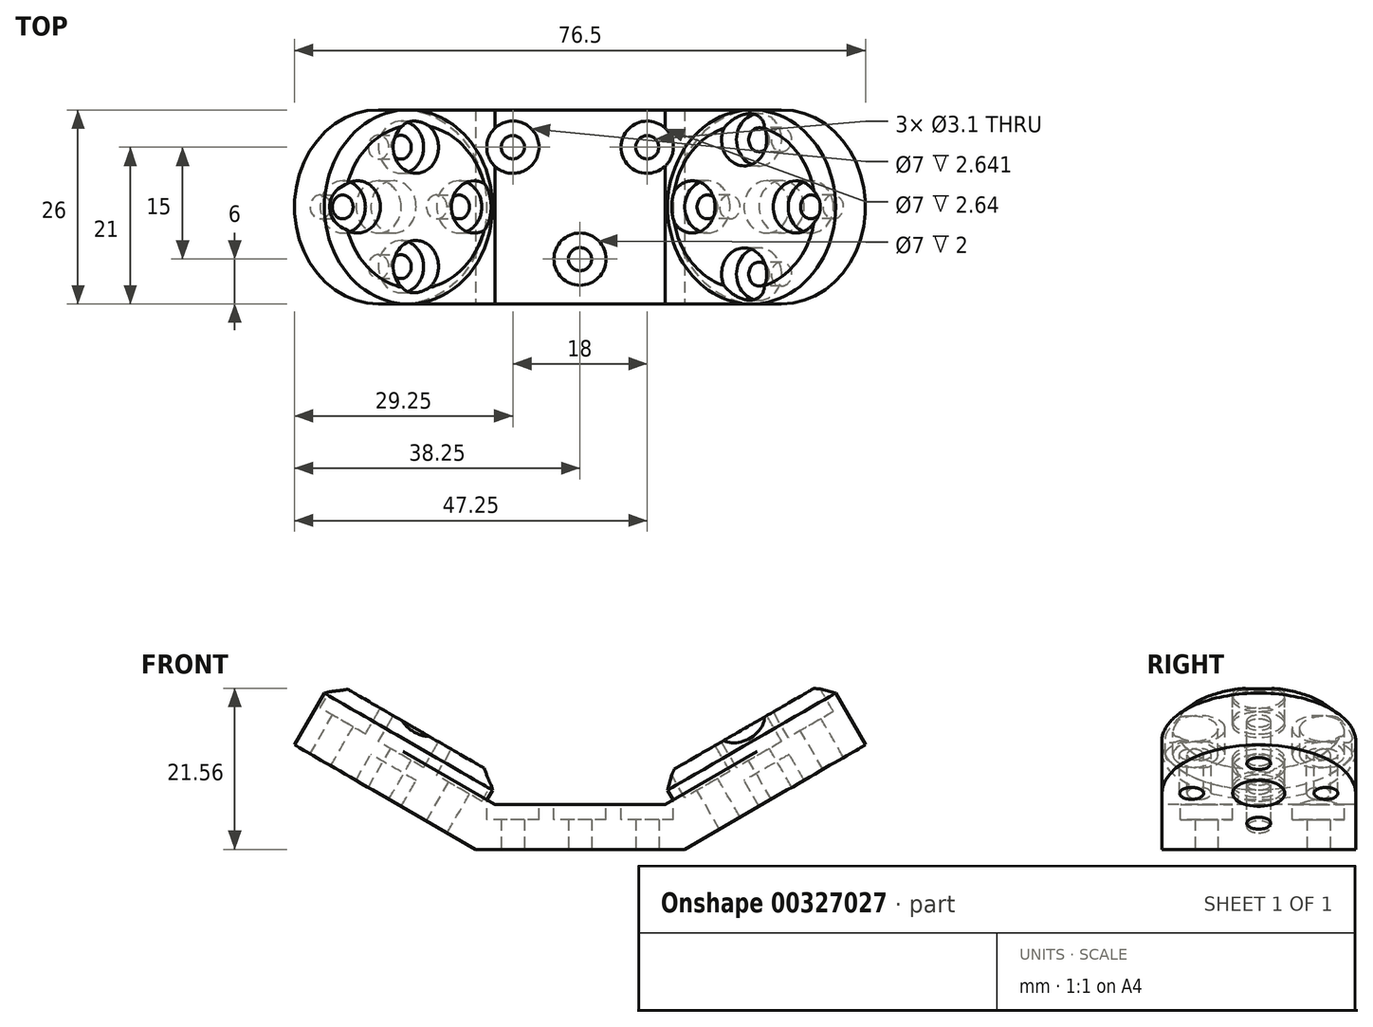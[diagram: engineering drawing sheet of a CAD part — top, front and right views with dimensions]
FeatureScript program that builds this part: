
annotation { "Feature Type Name" : "Feature", "Feature Type Description" : "" }
export const myFeature = defineFeature(function(context is Context, id is Id, definition is map)
    precondition{}
    {
        {
            var Q0;
            Q0=qCreatedBy(makeId("Top.planeOp"),FACE);
            var sketch = newSketch(context, id + "F0", { "sketchPlane" : qUnion([Q0])});
            skLineSegment(sketch, "E0.bottom", {"start": v(14, 13) * mm, "end": v(-14, 13) * mm});
            skLineSegment(sketch, "E0.top", {"start": v(14, -13) * mm, "end": v(-14, -13) * mm});
            skLineSegment(sketch, "E0.left", {"start": v(14, 13) * mm, "end": v(14, -13) * mm});
            skLineSegment(sketch, "E0.right", {"start": v(-14, 13) * mm, "end": v(-14, -13) * mm});
            skPoint(sketch, "E0.middle", {"position": v(0, 0) * mm});
            skCircle(sketch, "E1", {"center": v(9, 8) * mm, "radius": 1.55 * mm});
            skCircle(sketch, "E2", {"center": v(0, -7) * mm, "radius": 1.55 * mm});
            skCircle(sketch, "E3.MirrorC", {"center": v(-9, 8) * mm, "radius": 1.55 * mm});
            skSolve(sketch);
        }
        {
            var Q0;
            Q0=makeQuery(id+"F0.imprint","IMPRINT",FACE,{"disambiguationData":[TD([[makeQuery(id+"F0.imprint","IMPRINT",EDGE,{"derivedFrom":sQuery(id+"F0.wireOp",EDGE,"E0.bottom")}),1.0]])]});
            extrude(context, id + "F1", {"entities" : qUnion([Q0]), "depth" : 6 * mm});
        }
        {
            var Q0;
            Q0=makeQuery(id+"F1.opExtrude","SWEPT_FACE",FACE,{"disambiguationData":[OSD([sQuery(id+"F0.wireOp",EDGE,"E0.top")])]});
            var sketch = newSketch(context, id + "F2", { "sketchPlane" : qUnion([Q0])});
            skLineSegment(sketch, "E4", {"start": v(14, 0) * mm, "end": v(31.32, 10) * mm});
            skSolve(sketch);
        }
        {
            var Q0;
            Q0=sQuery(id+"F2.wireOp",EDGE,"E4");
            var Q1;
            Q1=makeQuery(id+"F1.opExtrude","SWEPT_FACE",FACE,{"disambiguationData":[OSD([sQuery(id+"F0.wireOp",EDGE,"E0.left")])]});
            cPlane(context, id + "F3", {"entities" : qUnion([Q0, Q1]), "cplaneType" : CPlaneType.LINE_ANGLE, "offset" : 25 * mm, "angle" : 0 * degree, "width" : 150 * mm, "height" : 150 * mm});
        }
        {
            var Q0;
            Q0=qCreatedBy(id+"F3.planeOp",FACE);
            var sketch = newSketch(context, id + "F4", { "sketchPlane" : qUnion([Q0])});
            skLineSegment(sketch, "E5", {"start": v(27.12, -13) * mm, "end": v(12.12, -13) * mm});
            skLineSegment(sketch, "E6", {"start": v(12.12, 13) * mm, "end": v(27.12, 13) * mm});
            skCircle(sketch, "E7", {"center": v(27.12, 0) * mm, "radius": 13 * mm});
            skLineSegment(sketch, "E8", {"start": v(12.12, 13) * mm, "end": v(12.12, -13) * mm});
            skSolve(sketch);
        }
        {
            var Q0;
            Q0 = qSketchRegion(id + "F4", true);
            extrude(context, id + "F5", {"entities" : qUnion([Q0]), "operationType" : NewBodyOperationType.ADD, "depth" : 6.5 * mm});
        }
        {
            var Q0;
            {var subQ0=sQuery(id+"F4.wireOp",EDGE,"E7");var subQ1=makeQuery(id+"F4.imprint","INTERSECT",VERTEX,{"derivedFrom":[sQuery(id+"F4.wireOp",EDGE,"E5"),subQ0]});Q0=makeQuery(id+"F4.imprint","IMPRINT",FACE,{"disambiguationData":[TD([[makeQuery(id+"F4.imprint","IMPRINT",EDGE,{"disambiguationData":[TD([[subQ1,1.0]])],"derivedFrom":subQ0}),1.0]])]});}
            extrude(context, id + "F6", {"entities" : qUnion([Q0]), "operationType" : NewBodyOperationType.ADD, "depth" : 10 * mm});
        }
        {
            var Q0;
            Q0=makeQuery(id+"F6.opExtrude","CAP_EDGE",EDGE,{"disambiguationData":[OSD([sQuery(id+"F4.wireOp",EDGE,"E7")])],"isStart":false});
            chamfer(context, id + "F7", {"entities" : qUnion([Q0]), "width" : 2 * mm, "tangentPropagation" : true});
        }
        {
            var Q0;
            Q0=makeQuery(id+"F1.opExtrude","SWEPT_BODY",BODY,{"disambiguationData":[OSD([sQuery(id+"F0.wireOp",EDGE,"E0.bottom"),sQuery(id+"F0.wireOp",EDGE,"E0.top"),sQuery(id+"F0.wireOp",EDGE,"E0.left"),sQuery(id+"F0.wireOp",EDGE,"E0.right"),sQuery(id+"F0.wireOp",EDGE,"E1"),sQuery(id+"F0.wireOp",EDGE,"E2"),sQuery(id+"F0.wireOp",EDGE,"E3.MirrorC")])]});
            var Q1;
            Q1=qCreatedBy(makeId("Right.planeOp"),FACE);
            mirror(context, id + "F8", {"operationType" : NewBodyOperationType.ADD, "entities" : qUnion([Q0]), "mirrorPlane" : qUnion([Q1])});
        }
        {
            var Q0;
            Q0=makeQuery(id+"F6.opExtrude","CAP_FACE",FACE,{"disambiguationData":[OSD([sQuery(id+"F4.wireOp",EDGE,"E7")])],"isStart":false});
            var sketch = newSketch(context, id + "F9", { "sketchPlane" : qUnion([Q0])});
            skCircle(sketch, "E9", {"center": v(27.12, 0) * mm, "radius": 3.5 * mm});
            skCircle(sketch, "E10", {"center": v(19.12, 0) * mm, "radius": 1.6 * mm});
            skCircle(sketch, "E11", {"center": v(35.12, 0) * mm, "radius": 1.6 * mm});
            skCircle(sketch, "E12", {"center": v(27.12, -9) * mm, "radius": 1.6 * mm});
            skCircle(sketch, "E13", {"center": v(27.12, 9) * mm, "radius": 1.6 * mm});
            skCircle(sketch, "E14", {"center": v(35.12, 0) * mm, "radius": 3.5 * mm});
            skCircle(sketch, "E15", {"center": v(27.12, -9) * mm, "radius": 3.5 * mm});
            skCircle(sketch, "E16", {"center": v(19.12, 0) * mm, "radius": 3.5 * mm});
            skCircle(sketch, "E17", {"center": v(27.12, 9) * mm, "radius": 3.5 * mm});
            skSolve(sketch);
        }
        {
            var Q0;
            Q0=makeQuery(id+"F9.imprint","IMPRINT",FACE,{"disambiguationData":[TD([[makeQuery(id+"F9.imprint","IMPRINT",EDGE,{"derivedFrom":sQuery(id+"F9.wireOp",EDGE,"E12")}),-1.0]])]});
            var Q1;
            {var subQ0=sQuery(id+"F9.wireOp",EDGE,"E15");var subQ1=sQuery(id+"F4.wireOp",EDGE,"E7");var subQ2=makeQuery(id+"F7.opChamfer","BLEND_EDGE",EDGE,{"blendedFrom":[makeQuery(id+"F6.opExtrude","CAP_EDGE",EDGE,{"disambiguationData":[OSD([subQ1])],"isStart":false}),makeQuery(id+"F6.opExtrude","CAP_FACE",FACE,{"disambiguationData":[OSD([subQ1])],"isStart":false})],"blendedInto":[makeQuery(id+"F6.opExtrude","CAP_FACE",FACE,{"disambiguationData":[OSD([subQ1])],"isStart":false})]});var subQ3=makeQuery(id+"F9.imprint","INTERSECT",VERTEX,{"disambiguationData":[OD(0.0)],"derivedFrom":[subQ2,subQ0]});Q1=makeQuery(id+"F9.imprint","IMPRINT",FACE,{"disambiguationData":[TD([[makeQuery(id+"F9.imprint","IMPRINT",EDGE,{"disambiguationData":[TD([[subQ3,-1.0]])],"derivedFrom":subQ0}),1.0]])]});}
            var Q2;
            Q2=makeQuery(id+"F9.imprint","IMPRINT",FACE,{"disambiguationData":[TD([[makeQuery(id+"F9.imprint","IMPRINT",EDGE,{"derivedFrom":sQuery(id+"F9.wireOp",EDGE,"E10")}),-1.0]])]});
            var Q3;
            {var subQ0=sQuery(id+"F9.wireOp",EDGE,"E16");var subQ1=sQuery(id+"F4.wireOp",EDGE,"E7");var subQ2=makeQuery(id+"F7.opChamfer","BLEND_EDGE",EDGE,{"blendedFrom":[makeQuery(id+"F6.opExtrude","CAP_EDGE",EDGE,{"disambiguationData":[OSD([subQ1])],"isStart":false}),makeQuery(id+"F6.opExtrude","CAP_FACE",FACE,{"disambiguationData":[OSD([subQ1])],"isStart":false})],"blendedInto":[makeQuery(id+"F6.opExtrude","CAP_FACE",FACE,{"disambiguationData":[OSD([subQ1])],"isStart":false})]});var subQ3=makeQuery(id+"F9.imprint","INTERSECT",VERTEX,{"disambiguationData":[OD(0.0)],"derivedFrom":[subQ2,subQ0]});Q3=makeQuery(id+"F9.imprint","IMPRINT",FACE,{"disambiguationData":[TD([[makeQuery(id+"F9.imprint","IMPRINT",EDGE,{"disambiguationData":[TD([[subQ3,1.0]])],"derivedFrom":subQ0}),1.0]])]});}
            var Q4;
            Q4=makeQuery(id+"F9.imprint","IMPRINT",FACE,{"disambiguationData":[TD([[makeQuery(id+"F9.imprint","IMPRINT",EDGE,{"derivedFrom":sQuery(id+"F9.wireOp",EDGE,"E13")}),-1.0]])]});
            var Q5;
            {var subQ0=sQuery(id+"F9.wireOp",EDGE,"E17");var subQ1=sQuery(id+"F4.wireOp",EDGE,"E7");var subQ2=makeQuery(id+"F7.opChamfer","BLEND_EDGE",EDGE,{"blendedFrom":[makeQuery(id+"F6.opExtrude","CAP_EDGE",EDGE,{"disambiguationData":[OSD([subQ1])],"isStart":false}),makeQuery(id+"F6.opExtrude","CAP_FACE",FACE,{"disambiguationData":[OSD([subQ1])],"isStart":false})],"blendedInto":[makeQuery(id+"F6.opExtrude","CAP_FACE",FACE,{"disambiguationData":[OSD([subQ1])],"isStart":false})]});var subQ3=makeQuery(id+"F9.imprint","INTERSECT",VERTEX,{"disambiguationData":[OD(0.0)],"derivedFrom":[subQ2,subQ0]});Q5=makeQuery(id+"F9.imprint","IMPRINT",FACE,{"disambiguationData":[TD([[makeQuery(id+"F9.imprint","IMPRINT",EDGE,{"disambiguationData":[TD([[subQ3,1.0]])],"derivedFrom":subQ0}),1.0]])]});}
            var Q6;
            Q6=makeQuery(id+"F9.imprint","IMPRINT",FACE,{"disambiguationData":[TD([[makeQuery(id+"F9.imprint","IMPRINT",EDGE,{"derivedFrom":sQuery(id+"F9.wireOp",EDGE,"E11")}),-1.0]])]});
            var Q7;
            {var subQ0=sQuery(id+"F9.wireOp",EDGE,"E14");var subQ1=sQuery(id+"F4.wireOp",EDGE,"E7");var subQ2=makeQuery(id+"F7.opChamfer","BLEND_EDGE",EDGE,{"blendedFrom":[makeQuery(id+"F6.opExtrude","CAP_EDGE",EDGE,{"disambiguationData":[OSD([subQ1])],"isStart":false}),makeQuery(id+"F6.opExtrude","CAP_FACE",FACE,{"disambiguationData":[OSD([subQ1])],"isStart":false})],"blendedInto":[makeQuery(id+"F6.opExtrude","CAP_FACE",FACE,{"disambiguationData":[OSD([subQ1])],"isStart":false})]});var subQ3=makeQuery(id+"F9.imprint","INTERSECT",VERTEX,{"disambiguationData":[OD(0.0)],"derivedFrom":[subQ2,subQ0]});Q7=makeQuery(id+"F9.imprint","IMPRINT",FACE,{"disambiguationData":[TD([[makeQuery(id+"F9.imprint","IMPRINT",EDGE,{"disambiguationData":[TD([[subQ3,-1.0]])],"derivedFrom":subQ0}),1.0]])]});}
            var Q8;
            Q8=makeQuery(id+"F9.imprint","IMPRINT",FACE,{"disambiguationData":[TD([[makeQuery(id+"F9.imprint","IMPRINT",EDGE,{"derivedFrom":sQuery(id+"F9.wireOp",EDGE,"E11")}),1.0]])]});
            var Q9;
            Q9=makeQuery(id+"F9.imprint","IMPRINT",FACE,{"disambiguationData":[TD([[makeQuery(id+"F9.imprint","IMPRINT",EDGE,{"derivedFrom":sQuery(id+"F9.wireOp",EDGE,"E10")}),1.0]])]});
            var Q10;
            Q10=makeQuery(id+"F9.imprint","IMPRINT",FACE,{"disambiguationData":[TD([[makeQuery(id+"F9.imprint","IMPRINT",EDGE,{"derivedFrom":sQuery(id+"F9.wireOp",EDGE,"E13")}),1.0]])]});
            var Q11;
            Q11=makeQuery(id+"F9.imprint","IMPRINT",FACE,{"disambiguationData":[TD([[makeQuery(id+"F9.imprint","IMPRINT",EDGE,{"derivedFrom":sQuery(id+"F9.wireOp",EDGE,"E12")}),1.0]])]});
            extrude(context, id + "F10", {"entities" : qUnion([Q0, Q1, Q2, Q3, Q4, Q5, Q6, Q7, Q8, Q9, Q10, Q11]), "operationType" : NewBodyOperationType.REMOVE, "oppositeDirection" : true, "depth" : 4 * mm});
        }
        {
            var Q0;
            Q0=makeQuery(id+"F9.imprint","IMPRINT",FACE,{"disambiguationData":[TD([[makeQuery(id+"F9.imprint","IMPRINT",EDGE,{"derivedFrom":sQuery(id+"F9.wireOp",EDGE,"E11")}),1.0]])]});
            var Q1;
            Q1=makeQuery(id+"F9.imprint","IMPRINT",FACE,{"disambiguationData":[TD([[makeQuery(id+"F9.imprint","IMPRINT",EDGE,{"derivedFrom":sQuery(id+"F9.wireOp",EDGE,"E10")}),1.0]])]});
            var Q2;
            Q2=makeQuery(id+"F9.imprint","IMPRINT",FACE,{"disambiguationData":[TD([[makeQuery(id+"F9.imprint","IMPRINT",EDGE,{"derivedFrom":sQuery(id+"F9.wireOp",EDGE,"E12")}),1.0]])]});
            var Q3;
            Q3=makeQuery(id+"F9.imprint","IMPRINT",FACE,{"disambiguationData":[TD([[makeQuery(id+"F9.imprint","IMPRINT",EDGE,{"derivedFrom":sQuery(id+"F9.wireOp",EDGE,"E13")}),1.0]])]});
            extrude(context, id + "F11", {"entities" : qUnion([Q0, Q1, Q2, Q3]), "operationType" : NewBodyOperationType.REMOVE, "oppositeDirection" : true, "depth" : 25 * mm});
        }
        {
            var Q0;
            Q0=makeQuery(id+"F9.imprint","IMPRINT",FACE,{"disambiguationData":[TD([[makeQuery(id+"F9.imprint","IMPRINT",EDGE,{"derivedFrom":sQuery(id+"F9.wireOp",EDGE,"E9")}),1.0]])]});
            extrude(context, id + "F12", {"entities" : qUnion([Q0]), "operationType" : NewBodyOperationType.REMOVE, "oppositeDirection" : true, "depth" : 25 * mm, "hasSecondDirection" : true, "secondDirectionOppositeDirection" : true, "secondDirectionDepth" : 6 * mm});
        }
        {
            var Q0;
            Q0=makeQuery(id+"F8.opPattern","COPY",FACE,{"derivedFrom":makeQuery(id+"F6.opExtrude","CAP_FACE",FACE,{"disambiguationData":[OSD([sQuery(id+"F4.wireOp",EDGE,"E7")])],"isStart":false}),"instanceName":"1"});
            var sketch = newSketch(context, id + "F13", { "sketchPlane" : qUnion([Q0])});
            skCircle(sketch, "E18", {"center": v(-27.12, 0) * mm, "radius": 3.5 * mm});
            skCircle(sketch, "E19", {"center": v(-36.12, 0) * mm, "radius": 1.6 * mm});
            skCircle(sketch, "E20", {"center": v(-18.12, 0) * mm, "radius": 1.6 * mm});
            skCircle(sketch, "E21", {"center": v(-27.12, -8) * mm, "radius": 1.6 * mm});
            skCircle(sketch, "E22", {"center": v(-27.12, 8) * mm, "radius": 1.6 * mm});
            skCircle(sketch, "E23", {"center": v(-27.12, -8) * mm, "radius": 3.5 * mm});
            skCircle(sketch, "E24", {"center": v(-36.12, 0) * mm, "radius": 3.5 * mm});
            skCircle(sketch, "E25", {"center": v(-27.12, 8) * mm, "radius": 3.5 * mm});
            skCircle(sketch, "E26", {"center": v(-18.12, 0) * mm, "radius": 3.5 * mm});
            skSolve(sketch);
        }
        {
            var Q0;
            Q0=makeQuery(id+"F13.imprint","IMPRINT",FACE,{"disambiguationData":[TD([[makeQuery(id+"F13.imprint","IMPRINT",EDGE,{"derivedFrom":sQuery(id+"F13.wireOp",EDGE,"E21")}),-1.0]])]});
            var Q1;
            Q1=makeQuery(id+"F13.imprint","IMPRINT",FACE,{"disambiguationData":[TD([[makeQuery(id+"F13.imprint","IMPRINT",EDGE,{"derivedFrom":sQuery(id+"F13.wireOp",EDGE,"E19")}),-1.0]])]});
            var Q2;
            Q2=makeQuery(id+"F13.imprint","IMPRINT",FACE,{"disambiguationData":[TD([[makeQuery(id+"F13.imprint","IMPRINT",EDGE,{"derivedFrom":sQuery(id+"F13.wireOp",EDGE,"E22")}),-1.0]])]});
            var Q3;
            Q3=makeQuery(id+"F13.imprint","IMPRINT",FACE,{"disambiguationData":[TD([[makeQuery(id+"F13.imprint","IMPRINT",EDGE,{"derivedFrom":sQuery(id+"F13.wireOp",EDGE,"E20")}),-1.0]])]});
            var Q4;
            Q4=makeQuery(id+"F13.imprint","IMPRINT",FACE,{"disambiguationData":[TD([[makeQuery(id+"F13.imprint","IMPRINT",EDGE,{"derivedFrom":sQuery(id+"F13.wireOp",EDGE,"E20")}),1.0]])]});
            var Q5;
            Q5=makeQuery(id+"F13.imprint","IMPRINT",FACE,{"disambiguationData":[TD([[makeQuery(id+"F13.imprint","IMPRINT",EDGE,{"derivedFrom":sQuery(id+"F13.wireOp",EDGE,"E22")}),1.0]])]});
            var Q6;
            Q6=makeQuery(id+"F13.imprint","IMPRINT",FACE,{"disambiguationData":[TD([[makeQuery(id+"F13.imprint","IMPRINT",EDGE,{"derivedFrom":sQuery(id+"F13.wireOp",EDGE,"E19")}),1.0]])]});
            var Q7;
            Q7=makeQuery(id+"F13.imprint","IMPRINT",FACE,{"disambiguationData":[TD([[makeQuery(id+"F13.imprint","IMPRINT",EDGE,{"derivedFrom":sQuery(id+"F13.wireOp",EDGE,"E21")}),1.0]])]});
            var Q8;
            {var subQ0=sQuery(id+"F13.wireOp",EDGE,"E23");var subQ1=sQuery(id+"F4.wireOp",EDGE,"E7");var subQ2=makeQuery(id+"F8.opPattern","COPY",EDGE,{"derivedFrom":makeQuery(id+"F7.opChamfer","BLEND_EDGE",EDGE,{"blendedFrom":[makeQuery(id+"F6.opExtrude","CAP_EDGE",EDGE,{"disambiguationData":[OSD([subQ1])],"isStart":false}),makeQuery(id+"F6.opExtrude","CAP_FACE",FACE,{"disambiguationData":[OSD([subQ1])],"isStart":false})],"blendedInto":[makeQuery(id+"F6.opExtrude","CAP_FACE",FACE,{"disambiguationData":[OSD([subQ1])],"isStart":false})]}),"instanceName":"1"});var subQ3=makeQuery(id+"F13.imprint","INTERSECT",VERTEX,{"disambiguationData":[OD(0.0)],"derivedFrom":[subQ2,subQ0]});Q8=makeQuery(id+"F13.imprint","IMPRINT",FACE,{"disambiguationData":[TD([[makeQuery(id+"F13.imprint","IMPRINT",EDGE,{"disambiguationData":[TD([[subQ3,-1.0]])],"derivedFrom":subQ0}),1.0]])]});}
            var Q9;
            {var subQ0=sQuery(id+"F13.wireOp",EDGE,"E24");var subQ1=sQuery(id+"F4.wireOp",EDGE,"E7");var subQ2=makeQuery(id+"F8.opPattern","COPY",EDGE,{"derivedFrom":makeQuery(id+"F7.opChamfer","BLEND_EDGE",EDGE,{"blendedFrom":[makeQuery(id+"F6.opExtrude","CAP_EDGE",EDGE,{"disambiguationData":[OSD([subQ1])],"isStart":false}),makeQuery(id+"F6.opExtrude","CAP_FACE",FACE,{"disambiguationData":[OSD([subQ1])],"isStart":false})],"blendedInto":[makeQuery(id+"F6.opExtrude","CAP_FACE",FACE,{"disambiguationData":[OSD([subQ1])],"isStart":false})]}),"instanceName":"1"});var subQ3=makeQuery(id+"F13.imprint","INTERSECT",VERTEX,{"disambiguationData":[OD(0.0)],"derivedFrom":[subQ2,subQ0]});Q9=makeQuery(id+"F13.imprint","IMPRINT",FACE,{"disambiguationData":[TD([[makeQuery(id+"F13.imprint","IMPRINT",EDGE,{"disambiguationData":[TD([[subQ3,1.0]])],"derivedFrom":subQ0}),1.0]])]});}
            var Q10;
            {var subQ0=sQuery(id+"F13.wireOp",EDGE,"E25");var subQ1=sQuery(id+"F4.wireOp",EDGE,"E7");var subQ2=makeQuery(id+"F8.opPattern","COPY",EDGE,{"derivedFrom":makeQuery(id+"F7.opChamfer","BLEND_EDGE",EDGE,{"blendedFrom":[makeQuery(id+"F6.opExtrude","CAP_EDGE",EDGE,{"disambiguationData":[OSD([subQ1])],"isStart":false}),makeQuery(id+"F6.opExtrude","CAP_FACE",FACE,{"disambiguationData":[OSD([subQ1])],"isStart":false})],"blendedInto":[makeQuery(id+"F6.opExtrude","CAP_FACE",FACE,{"disambiguationData":[OSD([subQ1])],"isStart":false})]}),"instanceName":"1"});var subQ3=makeQuery(id+"F13.imprint","INTERSECT",VERTEX,{"disambiguationData":[OD(0.0)],"derivedFrom":[subQ2,subQ0]});Q10=makeQuery(id+"F13.imprint","IMPRINT",FACE,{"disambiguationData":[TD([[makeQuery(id+"F13.imprint","IMPRINT",EDGE,{"disambiguationData":[TD([[subQ3,1.0]])],"derivedFrom":subQ0}),1.0]])]});}
            var Q11;
            {var subQ0=sQuery(id+"F13.wireOp",EDGE,"E26");var subQ1=sQuery(id+"F4.wireOp",EDGE,"E7");var subQ2=makeQuery(id+"F8.opPattern","COPY",EDGE,{"derivedFrom":makeQuery(id+"F7.opChamfer","BLEND_EDGE",EDGE,{"blendedFrom":[makeQuery(id+"F6.opExtrude","CAP_EDGE",EDGE,{"disambiguationData":[OSD([subQ1])],"isStart":false}),makeQuery(id+"F6.opExtrude","CAP_FACE",FACE,{"disambiguationData":[OSD([subQ1])],"isStart":false})],"blendedInto":[makeQuery(id+"F6.opExtrude","CAP_FACE",FACE,{"disambiguationData":[OSD([subQ1])],"isStart":false})]}),"instanceName":"1"});var subQ3=makeQuery(id+"F13.imprint","INTERSECT",VERTEX,{"disambiguationData":[OD(0.0)],"derivedFrom":[subQ2,subQ0]});Q11=makeQuery(id+"F13.imprint","IMPRINT",FACE,{"disambiguationData":[TD([[makeQuery(id+"F13.imprint","IMPRINT",EDGE,{"disambiguationData":[TD([[subQ3,-1.0]])],"derivedFrom":subQ0}),1.0]])]});}
            extrude(context, id + "F14", {"entities" : qUnion([Q0, Q1, Q2, Q3, Q4, Q5, Q6, Q7, Q8, Q9, Q10, Q11]), "operationType" : NewBodyOperationType.REMOVE, "oppositeDirection" : true, "depth" : 4 * mm});
        }
        {
            var Q0;
            Q0=makeQuery(id+"F13.imprint","IMPRINT",FACE,{"disambiguationData":[TD([[makeQuery(id+"F13.imprint","IMPRINT",EDGE,{"derivedFrom":sQuery(id+"F13.wireOp",EDGE,"E20")}),1.0]])]});
            var Q1;
            Q1=makeQuery(id+"F13.imprint","IMPRINT",FACE,{"disambiguationData":[TD([[makeQuery(id+"F13.imprint","IMPRINT",EDGE,{"derivedFrom":sQuery(id+"F13.wireOp",EDGE,"E21")}),1.0]])]});
            var Q2;
            Q2=makeQuery(id+"F13.imprint","IMPRINT",FACE,{"disambiguationData":[TD([[makeQuery(id+"F13.imprint","IMPRINT",EDGE,{"derivedFrom":sQuery(id+"F13.wireOp",EDGE,"E19")}),1.0]])]});
            var Q3;
            Q3=makeQuery(id+"F13.imprint","IMPRINT",FACE,{"disambiguationData":[TD([[makeQuery(id+"F13.imprint","IMPRINT",EDGE,{"derivedFrom":sQuery(id+"F13.wireOp",EDGE,"E22")}),1.0]])]});
            extrude(context, id + "F15", {"entities" : qUnion([Q0, Q1, Q2, Q3]), "operationType" : NewBodyOperationType.REMOVE, "oppositeDirection" : true, "depth" : 25 * mm});
        }
        {
            var Q0;
            Q0=makeQuery(id+"F13.imprint","IMPRINT",FACE,{"disambiguationData":[TD([[makeQuery(id+"F13.imprint","IMPRINT",EDGE,{"derivedFrom":sQuery(id+"F13.wireOp",EDGE,"E18")}),1.0]])]});
            extrude(context, id + "F16", {"entities" : qUnion([Q0]), "operationType" : NewBodyOperationType.REMOVE, "oppositeDirection" : true, "depth" : 25 * mm, "hasSecondDirection" : true, "secondDirectionOppositeDirection" : true, "secondDirectionDepth" : 6 * mm});
        }
        {
            var Q0;
            Q0=makeQuery(id+"F1.opExtrude","CAP_FACE",FACE,{"disambiguationData":[OSD([sQuery(id+"F0.wireOp",EDGE,"E0.bottom"),sQuery(id+"F0.wireOp",EDGE,"E0.top"),sQuery(id+"F0.wireOp",EDGE,"E0.left"),sQuery(id+"F0.wireOp",EDGE,"E0.right"),sQuery(id+"F0.wireOp",EDGE,"E1"),sQuery(id+"F0.wireOp",EDGE,"E2"),sQuery(id+"F0.wireOp",EDGE,"E3.MirrorC")])],"isStart":false});
            var sketch = newSketch(context, id + "F17", { "sketchPlane" : qUnion([Q0])});
            skCircle(sketch, "E27", {"center": v(-9, 8) * mm, "radius": 3.5 * mm});
            skCircle(sketch, "E28", {"center": v(9, 8) * mm, "radius": 3.5 * mm});
            skCircle(sketch, "E29", {"center": v(0, -7) * mm, "radius": 3.5 * mm});
            skSolve(sketch);
        }
        {
            var Q0;
            Q0 = qSketchRegion(id + "F17", true);
            extrude(context, id + "F18", {"entities" : qUnion([Q0]), "operationType" : NewBodyOperationType.REMOVE, "oppositeDirection" : true, "depth" : 2 * mm});
        }
        {
            var Q0;
            Q0 = qSketchRegion(id + "F17", true);
            extrude(context, id + "F19", {"entities" : qUnion([Q0]), "operationType" : NewBodyOperationType.REMOVE, "depth" : 25 * mm});
        }
    });
